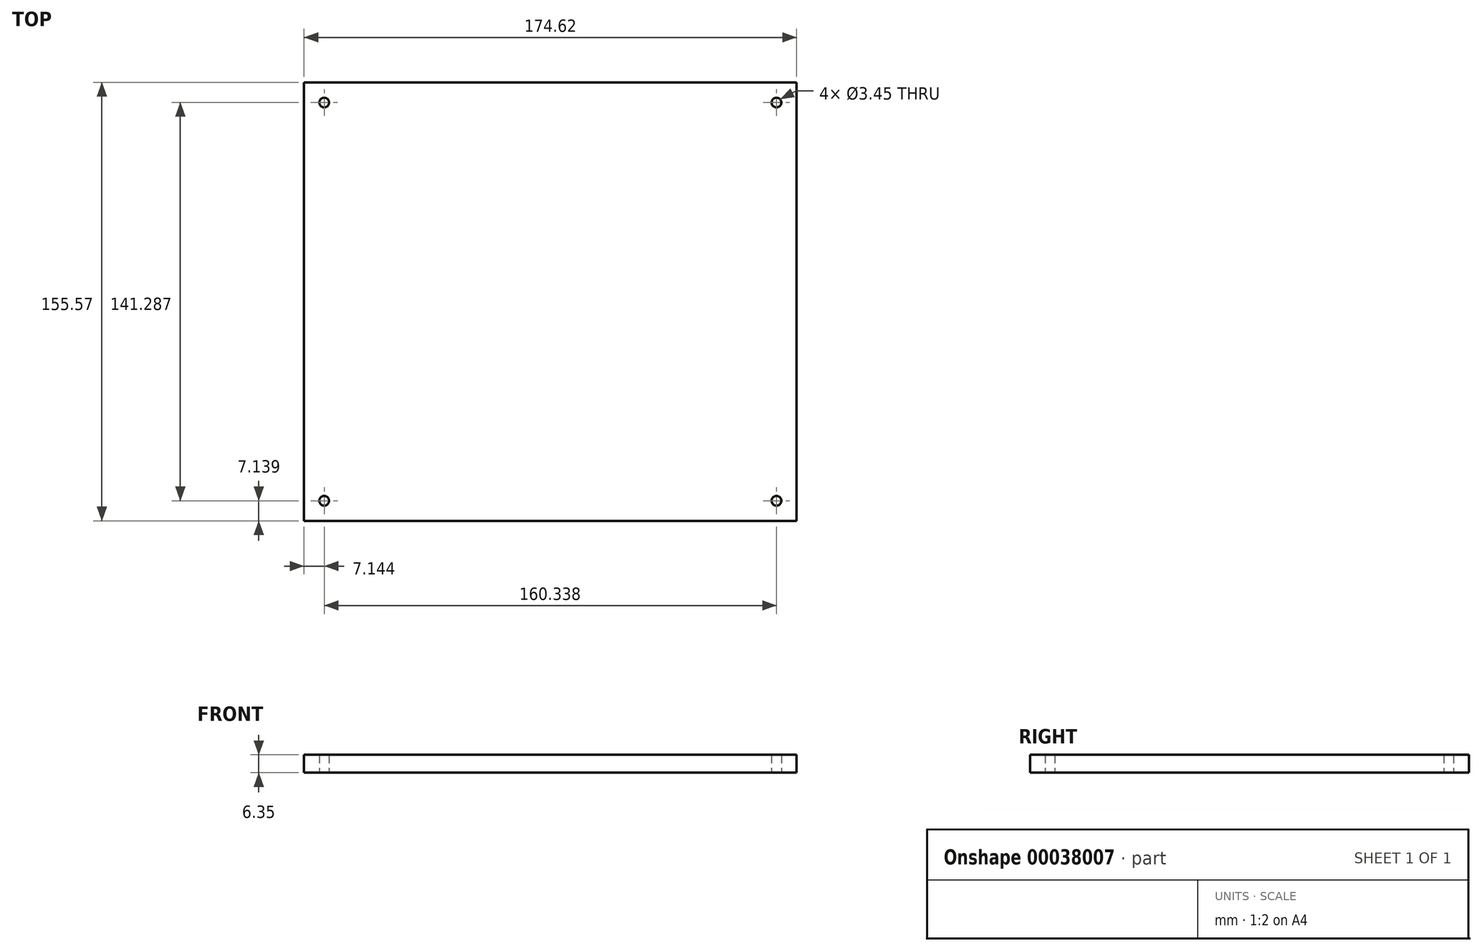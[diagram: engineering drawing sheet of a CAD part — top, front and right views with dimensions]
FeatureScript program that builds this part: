
annotation { "Feature Type Name" : "Feature", "Feature Type Description" : "" }
export const myFeature = defineFeature(function(context is Context, id is Id, definition is map)
    precondition{}
    {
        {
            var Q0;
            Q0=qCreatedBy(makeId("Top.planeOp"),FACE);
            var sketch = newSketch(context, id + "F0", { "sketchPlane" : qUnion([Q0])});
            skLineSegment(sketch, "E0.bottom", {"start": v(0, 0) * mm, "end": v(174.62, 0) * mm});
            skLineSegment(sketch, "E0.top", {"start": v(0, -155.58) * mm, "end": v(174.62, -155.57) * mm});
            skLineSegment(sketch, "E0.left", {"start": v(0, 0) * mm, "end": v(0, -155.58) * mm});
            skLineSegment(sketch, "E0.right", {"start": v(174.63, 0) * mm, "end": v(174.62, -155.57) * mm});
            skLineSegment(sketch, "E1", {"start": v(167.48, 0) * mm, "end": v(167.48, -7.14) * mm, "construction": true});
            skLineSegment(sketch, "E2", {"start": v(167.48, -7.14) * mm, "end": v(174.63, -7.14) * mm, "construction": true});
            skLineSegment(sketch, "E3", {"start": v(167.48, -155.57) * mm, "end": v(167.48, -148.43) * mm, "construction": true});
            skLineSegment(sketch, "E4", {"start": v(7.14, -155.57) * mm, "end": v(7.14, -148.43) * mm, "construction": true});
            skLineSegment(sketch, "E5", {"start": v(7.14, 0) * mm, "end": v(7.14, -7.14) * mm, "construction": true});
            skLineSegment(sketch, "E6", {"start": v(7.14, -7.14) * mm, "end": v(0, -7.14) * mm, "construction": true});
            skCircle(sketch, "E7", {"center": v(7.14, -7.14) * mm, "radius": 1.73 * mm});
            skCircle(sketch, "E8", {"center": v(167.48, -7.14) * mm, "radius": 1.73 * mm});
            skCircle(sketch, "E9", {"center": v(167.48, -148.43) * mm, "radius": 1.73 * mm});
            skCircle(sketch, "E10", {"center": v(7.14, -148.43) * mm, "radius": 1.73 * mm});
            skSolve(sketch);
        }
        {
            var Q0;
            Q0 = qSketchRegion(id + "F0", true);
            extrude(context, id + "F1", {"entities" : qUnion([Q0]), "depth" : 6.35 * mm});
        }
    });
